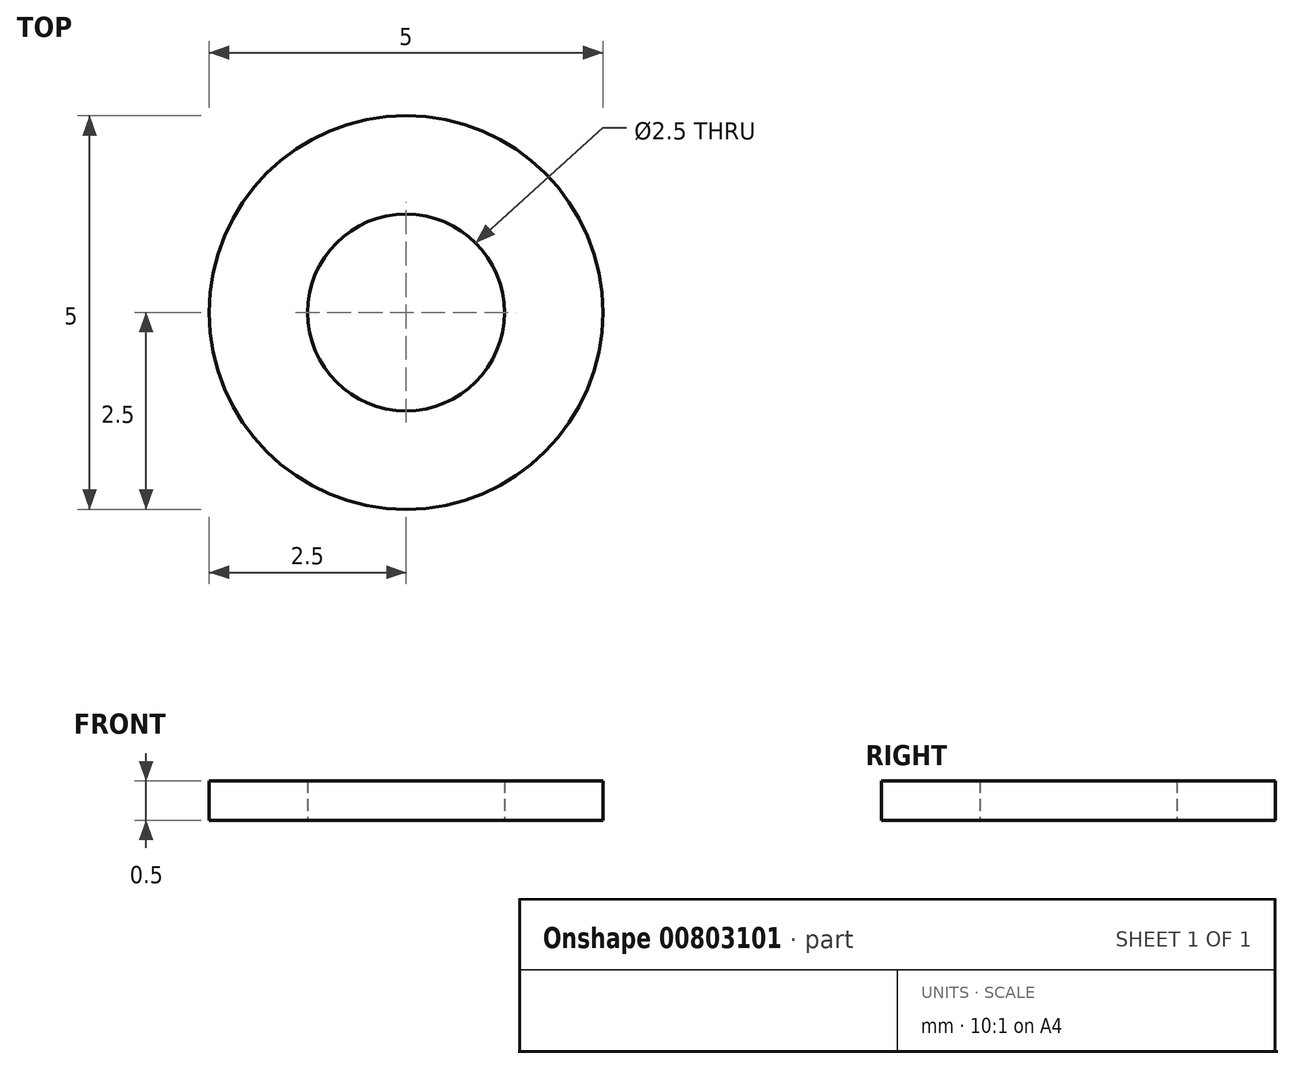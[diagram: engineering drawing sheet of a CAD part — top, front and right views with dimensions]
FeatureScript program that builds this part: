
annotation { "Feature Type Name" : "Feature", "Feature Type Description" : "" }
export const myFeature = defineFeature(function(context is Context, id is Id, definition is map)
    precondition{}
    {
        {
            var Q0;
            Q0=qCreatedBy(makeId("Top.planeOp"),FACE);
            var sketch = newSketch(context, id + "F0", { "sketchPlane" : qUnion([Q0])});
            skCircle(sketch, "E0", {"center": v(0, 0) * mm, "radius": 2.5 * mm});
            skCircle(sketch, "E1", {"center": v(0, 0) * mm, "radius": 1.25 * mm});
            skSolve(sketch);
        }
        {
            var Q0;
            Q0=makeQuery(id+"F0.imprint","IMPRINT",FACE,{"disambiguationData":[TD([[makeQuery(id+"F0.imprint","IMPRINT",EDGE,{"derivedFrom":sQuery(id+"F0.wireOp",EDGE,"E0")}),1.0]])]});
            extrude(context, id + "F1", {"entities" : qUnion([Q0]), "depth" : 0.5 * mm, "offsetDistance" : 25 * mm});
        }
    });
